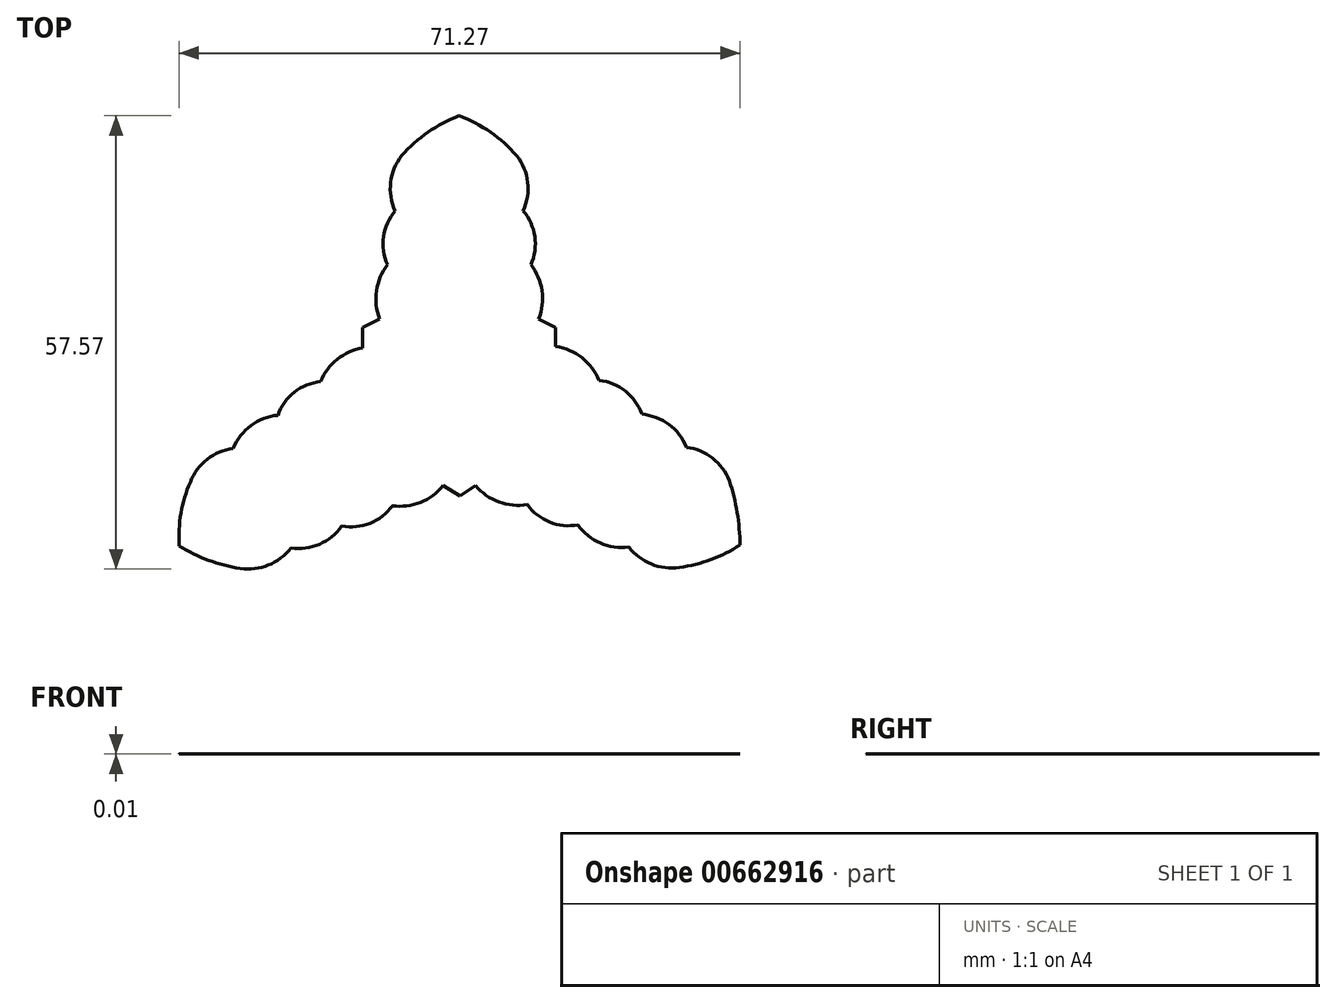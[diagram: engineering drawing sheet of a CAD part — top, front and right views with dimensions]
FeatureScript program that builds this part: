
annotation { "Feature Type Name" : "Feature", "Feature Type Description" : "" }
export const myFeature = defineFeature(function(context is Context, id is Id, definition is map)
    precondition{}
    {
        {
            var Q0;
            Q0=qCreatedBy(makeId("Top.planeOp"),FACE);
            var sketch = newSketch(context, id + "F0", { "sketchPlane" : qUnion([Q0])});
            skPoint(sketch, "E0.center", {"position": v(0, 0) * mm});
            skArc(sketch, "E1", {"start": v(-7.42, 28.98) * mm, "mid": v(-8.81, 25.6) * mm, "end": v(-8.23, 21.98) * mm});
            skArc(sketch, "E2", {"start": v(-8.23, 21.98) * mm, "mid": v(-9.72, 18.7) * mm, "end": v(-9.2, 15.13) * mm});
            skArc(sketch, "E3", {"start": v(-9.2, 15.13) * mm, "mid": v(-10.62, 11.82) * mm, "end": v(-10.2, 8.25) * mm});
            skLineSegment(sketch, "E4", {"start": v(-10.2, 8.25) * mm, "end": v(-12.37, 7.15) * mm});
            skLineSegment(sketch, "E5", {"start": v(-12.37, 7.15) * mm, "end": v(-12.37, 4.64) * mm});
            skLineSegment(sketch, "E6.MirrorCS", {"start": v(12.16, 7.15) * mm, "end": v(12.16, 4.64) * mm});
            skLineSegment(sketch, "E7.MirrorCS", {"start": v(10, 8.25) * mm, "end": v(12.16, 7.15) * mm});
            skArc(sketch, "E8.MirrorCS", {"start": v(9, 15.13) * mm, "mid": v(10.4, 11.82) * mm, "end": v(10, 8.25) * mm});
            skArc(sketch, "E9.MirrorCS", {"start": v(8.01, 21.98) * mm, "mid": v(9.5, 18.7) * mm, "end": v(9, 15.13) * mm});
            skArc(sketch, "E10.MirrorCS", {"start": v(7.2, 28.98) * mm, "mid": v(8.6, 25.6) * mm, "end": v(8.01, 21.98) * mm});
            skArc(sketch, "E11", {"start": v(34.22, -12.32) * mm, "mid": v(32.07, -9.44) * mm, "end": v(28.76, -8.05) * mm});
            skArc(sketch, "E12", {"start": v(28.76, -8.05) * mm, "mid": v(26.53, -5.15) * mm, "end": v(23.1, -3.85) * mm});
            skArc(sketch, "E13", {"start": v(23.1, -3.85) * mm, "mid": v(21, -0.92) * mm, "end": v(17.66, 0.43) * mm});
            skArc(sketch, "E14", {"start": v(17.66, 0.43) * mm, "mid": v(15.48, 3.32) * mm, "end": v(12.16, 4.74) * mm});
            skArc(sketch, "E15.MirrorCS", {"start": v(8.56, -15.34) * mm, "mid": v(4.94, -15) * mm, "end": v(1.97, -12.9) * mm});
            skArc(sketch, "E16.MirrorCS", {"start": v(14.98, -17.91) * mm, "mid": v(11.4, -17.56) * mm, "end": v(8.56, -15.34) * mm});
            skArc(sketch, "E17.MirrorCS", {"start": v(21.45, -20.71) * mm, "mid": v(17.82, -20.23) * mm, "end": v(14.98, -17.91) * mm});
            skArc(sketch, "E18.MirrorCS", {"start": v(27.87, -23.3) * mm, "mid": v(24.3, -22.89) * mm, "end": v(21.45, -20.71) * mm});
            skLineSegment(sketch, "E19", {"start": v(1.97, -12.9) * mm, "end": v(0, -14.26) * mm});
            skLineSegment(sketch, "E20", {"start": v(0, -14.26) * mm, "end": v(-2.14, -12.9) * mm});
            skArc(sketch, "E21", {"start": v(-27.91, -23.45) * mm, "mid": v(-24.35, -23.03) * mm, "end": v(-21.5, -20.86) * mm});
            skArc(sketch, "E22", {"start": v(-21.5, -20.86) * mm, "mid": v(-17.86, -20.37) * mm, "end": v(-15.02, -18.05) * mm});
            skArc(sketch, "E23", {"start": v(-15.02, -18.05) * mm, "mid": v(-11.43, -17.7) * mm, "end": v(-8.6, -15.48) * mm});
            skArc(sketch, "E24", {"start": v(-8.6, -15.48) * mm, "mid": v(-5.03, -15.05) * mm, "end": v(-2.14, -12.9) * mm});
            skArc(sketch, "E25.MirrorCS", {"start": v(-17.7, 0.28) * mm, "mid": v(-15.6, 3.12) * mm, "end": v(-12.37, 4.57) * mm});
            skArc(sketch, "E26.MirrorCS", {"start": v(-23.14, -4) * mm, "mid": v(-21.05, -1.06) * mm, "end": v(-17.7, 0.28) * mm});
            skArc(sketch, "E27.MirrorCS", {"start": v(-28.8, -8.2) * mm, "mid": v(-26.56, -5.3) * mm, "end": v(-23.14, -4) * mm});
            skArc(sketch, "E28.MirrorCS", {"start": v(-34.25, -12.46) * mm, "mid": v(-32.11, -9.58) * mm, "end": v(-28.8, -8.2) * mm});
            skLineSegment(sketch, "E29", {"start": v(-12.37, 4.64) * mm, "end": v(-12.37, 4.57) * mm});
            skArc(sketch, "E30", {"start": v(-34.25, -12.46) * mm, "mid": v(-35.45, -16.43) * mm, "end": v(-35.66, -20.56) * mm});
            skArc(sketch, "E31", {"start": v(-35.66, -20.56) * mm, "mid": v(-31.94, -22.42) * mm, "end": v(-27.91, -23.45) * mm});
            skArc(sketch, "E32", {"start": v(35.57, -20.47) * mm, "mid": v(35.2, -16.34) * mm, "end": v(34.22, -12.32) * mm});
            skArc(sketch, "E33", {"start": v(27.87, -23.3) * mm, "mid": v(31.88, -22.33) * mm, "end": v(35.57, -20.47) * mm});
            skArc(sketch, "E34", {"start": v(-0.1, 34.05) * mm, "mid": v(-4.07, 31.97) * mm, "end": v(-7.42, 28.98) * mm});
            skArc(sketch, "E35", {"start": v(7.2, 28.98) * mm, "mid": v(3.87, 31.97) * mm, "end": v(-0.1, 34.05) * mm});
            skSolve(sketch);
        }
        {
            var Q0;
            Q0=makeQuery(id+"F0.imprint","IMPRINT",FACE,{"disambiguationData":[TD([[makeQuery(id+"F0.imprint","IMPRINT",EDGE,{"derivedFrom":sQuery(id+"F0.wireOp",EDGE,"E1")}),1.0]])]});
            extrude(context, id + "F1", {"entities" : qUnion([Q0]), "depth" : 5 / 406.4 * mm, "offsetDistance" : 25.4 * mm});
        }
    });
